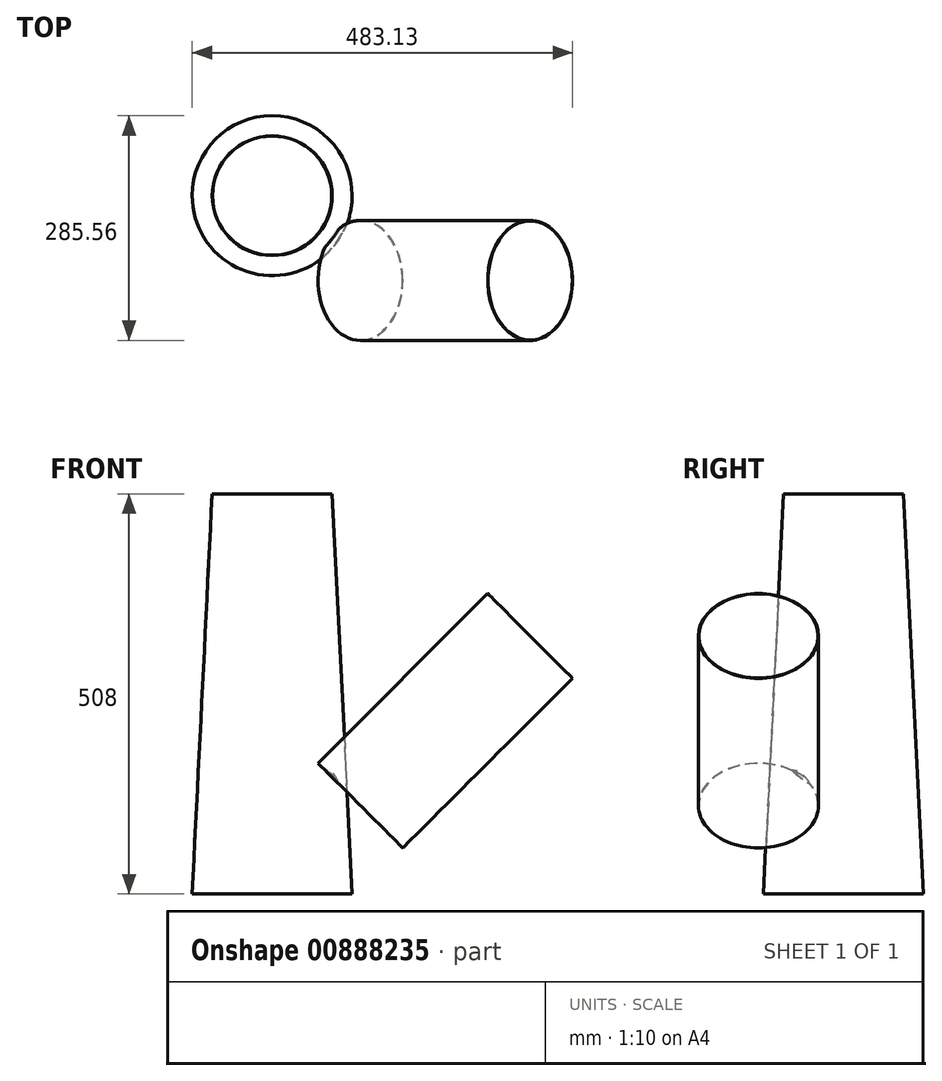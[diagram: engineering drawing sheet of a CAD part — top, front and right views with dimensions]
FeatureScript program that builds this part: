
annotation { "Feature Type Name" : "Feature", "Feature Type Description" : "" }
export const myFeature = defineFeature(function(context is Context, id is Id, definition is map)
    precondition{}
    {
        {
            var Q0;
            Q0=qCreatedBy(makeId("Front.planeOp"),FACE);
            var sketch = newSketch(context, id + "F0", { "sketchPlane" : qUnion([Q0])});
            skLineSegment(sketch, "E0", {"start": v(0, 0) * mm, "end": v(0, 508) * mm});
            skLineSegment(sketch, "E1", {"start": v(0, 508) * mm, "end": v(0, 254) * mm});
            skLineSegment(sketch, "E2", {"start": v(0, 152.4) * mm, "end": v(251.45, 403.85) * mm});
            skPoint(sketch, "E3", {"position": v(251.45, 403.85) * mm});
            skSolve(sketch);
        }
        {
            var Q0;
            Q0=sQuery(id+"F0.wireOp",VERTEX,"E0.start");
            var Q1;
            Q1=sQuery(id+"F0.wireOp",EDGE,"E0");
            cPlane(context, id + "F1", {"entities" : qUnion([Q0, Q1]), "cplaneType" : CPlaneType.LINE_POINT, "offset" : 25.4 * mm, "width" : 152.4 * mm, "height" : 152.4 * mm});
        }
        {
            var Q0;
            Q0=sQuery(id+"F0.wireOp",VERTEX,"E0.end");
            var Q1;
            Q1=sQuery(id+"F0.wireOp",EDGE,"E1");
            cPlane(context, id + "F2", {"entities" : qUnion([Q0, Q1]), "cplaneType" : CPlaneType.LINE_POINT, "offset" : 25.4 * mm, "width" : 152.4 * mm, "height" : 152.4 * mm});
        }
        {
            var Q0;
            Q0=sQuery(id+"F0.wireOp",VERTEX,"E2.end");
            var Q1;
            Q1=sQuery(id+"F0.wireOp",EDGE,"E2");
            cPlane(context, id + "F3", {"entities" : qUnion([Q0, Q1]), "cplaneType" : CPlaneType.LINE_POINT, "offset" : 25.4 * mm, "width" : 152.4 * mm, "height" : 152.4 * mm});
        }
        {
            var Q0;
            Q0=qCreatedBy(id+"F1.planeOp",FACE);
            var sketch = newSketch(context, id + "F4", { "sketchPlane" : qUnion([Q0])});
            skCircle(sketch, "E4", {"center": v(0, 0) * mm, "radius": 101.6 * mm});
            skSolve(sketch);
        }
        {
            var Q0;
            Q0=qCreatedBy(id+"F2.planeOp",FACE);
            var sketch = newSketch(context, id + "F5", { "sketchPlane" : qUnion([Q0])});
            skCircle(sketch, "E5", {"center": v(0, 0) * mm, "radius": 76.2 * mm});
            skSolve(sketch);
        }
        {
            var Q0;
            Q0=makeQuery(id+"F5.imprint","IMPRINT",FACE,{"disambiguationData":[TD([[makeQuery(id+"F5.imprint","IMPRINT",EDGE,{"derivedFrom":sQuery(id+"F5.wireOp",EDGE,"E5")}),1.0]])]});
            var Q1;
            Q1=makeQuery(id+"F4.imprint","IMPRINT",FACE,{"disambiguationData":[TD([[makeQuery(id+"F4.imprint","IMPRINT",EDGE,{"derivedFrom":sQuery(id+"F4.wireOp",EDGE,"E4")}),1.0]])]});
            var Q2;
            Q2=sQuery(id+"F4.wireOp",EDGE,"E4");
            var Q3;
            Q3=sQuery(id+"F5.wireOp",EDGE,"E5");
            loft(context, id + "F6", {"sheetProfilesArray" : [{ "sheetProfileEntities" : qUnion([Q0]) }, { "sheetProfileEntities" : qUnion([Q1]) }], "wireProfilesArray" : [{ "wireProfileEntities" : qUnion([Q2]) }, { "wireProfileEntities" : qUnion([Q3]) }]});
        }
        {
            var Q0;
            Q0=qCreatedBy(id+"F3.planeOp",FACE);
            var sketch = newSketch(context, id + "F7", { "sketchPlane" : qUnion([Q0])});
            skPoint(sketch, "E6", {"position": v(-107.76, 0) * mm});
            skCircle(sketch, "E7", {"center": v(-107.76, 0) * mm, "radius": 76.2 * mm});
            skSolve(sketch);
        }
        {
            var Q0;
            Q0=makeQuery(id+"F7.imprint","IMPRINT",FACE,{"disambiguationData":[TD([[makeQuery(id+"F7.imprint","IMPRINT",EDGE,{"derivedFrom":sQuery(id+"F7.wireOp",EDGE,"E7")}),1.0]])]});
            extrude(context, id + "F8", {"entities" : qUnion([Q0]), "operationType" : NewBodyOperationType.ADD, "oppositeDirection" : true, "depth" : 304.8 * mm, "offsetDistance" : 25.4 * mm});
        }
        {
            var Q0;
            Q0=makeQuery(id+"F7.imprint","IMPRINT",FACE,{"disambiguationData":[TD([[makeQuery(id+"F7.imprint","IMPRINT",EDGE,{"derivedFrom":sQuery(id+"F7.wireOp",EDGE,"E7")}),1.0]])]});
            var sketch = newSketch(context, id + "F9", { "sketchPlane" : qUnion([Q0])});
            skCircle(sketch, "E8", {"center": v(-107.76, 0) * mm, "radius": 75.72 * mm});
            skSolve(sketch);
        }
        {
            var Q0;
            Q0=makeQuery(id+"F5.imprint","IMPRINT",FACE,{"disambiguationData":[TD([[makeQuery(id+"F5.imprint","IMPRINT",EDGE,{"derivedFrom":sQuery(id+"F5.wireOp",EDGE,"E5")}),1.0]])]});
            var sketch = newSketch(context, id + "F10", { "sketchPlane" : qUnion([Q0])});
            skCircle(sketch, "E9", {"center": v(0, 0) * mm, "radius": 75.72 * mm});
            skSolve(sketch);
        }
        {
            var Q0;
            Q0=makeQuery(id+"F4.imprint","IMPRINT",FACE,{"disambiguationData":[TD([[makeQuery(id+"F4.imprint","IMPRINT",EDGE,{"derivedFrom":sQuery(id+"F4.wireOp",EDGE,"E4")}),1.0]])]});
            var sketch = newSketch(context, id + "F11", { "sketchPlane" : qUnion([Q0])});
            skCircle(sketch, "E10", {"center": v(0, 0) * mm, "radius": 101.12 * mm});
            skSolve(sketch);
        }
        {
            var Q0;
            Q0 = qSketchRegion(id + "F9", true);
            extrude(context, id + "F12", {"entities" : qUnion([Q0]), "operationType" : NewBodyOperationType.REMOVE, "oppositeDirection" : true, "depth" : 304.8 * mm, "offsetDistance" : 25.4 * mm});
        }
        {
            var Q1;
            Q1 = qSketchRegion(id + "F10", true);
            var Q2;
            Q2 = qSketchRegion(id + "F11", true);
            loft(context, id + "F13", {"operationType" : NewBodyOperationType.REMOVE, "sheetProfilesArray" : [{ "sheetProfileEntities" : qUnion([Q1]) }, { "sheetProfileEntities" : qUnion([Q2]) }]});
        }
    });
